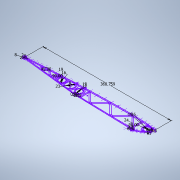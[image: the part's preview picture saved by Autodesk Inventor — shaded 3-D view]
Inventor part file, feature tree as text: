
AUTODESK INVENTOR PART (.ipt)
format: ipt  version: 2022 (Build 260153000, 153)  size: 268,800 bytes
history: native  units: mm
features: sketch x1
ambient origin geometry x8: Origin, YZ Plane, XZ Plane, XY Plane, X Axis, Y Axis, Z Axis, Center Point
feature tree (1):
  sketch  "Sketch1"  dims[d31=34.456mm d50=368.759386mm d57=16.0mm d69=8.0mm d70=23.0mm d71=8.0mm d73=16.0mm d80=19.0mm d81=16.0mm d82=1.0mm d83=1.0mm d84=1.0mm d85=1.0mm d86=1.0mm d87=0.8mm d88=1.0mm d90=19.0mm d94=5.0mm d95=5.0mm d105=5.0mm d106=5.0mm d108=2.0mm d109=19.0mm d114=5.0mm d115=5.0mm d116=24.0mm d117=2.5mm d118=2.5mm d123=2.5mm d124=2.5mm d125=10.0mm d126=24.0mm d127=24.0mm d128=27.0mm d135=0.5mm d136=45.0deg d139=7.0mm d165=45.0deg d169=27.0mm d175=90.0deg d181=45.0deg d185=7.0mm d186=45.0deg d190=7.0mm d191=45.0deg d197=90.0deg d203=90.0deg d206=7.0mm]
